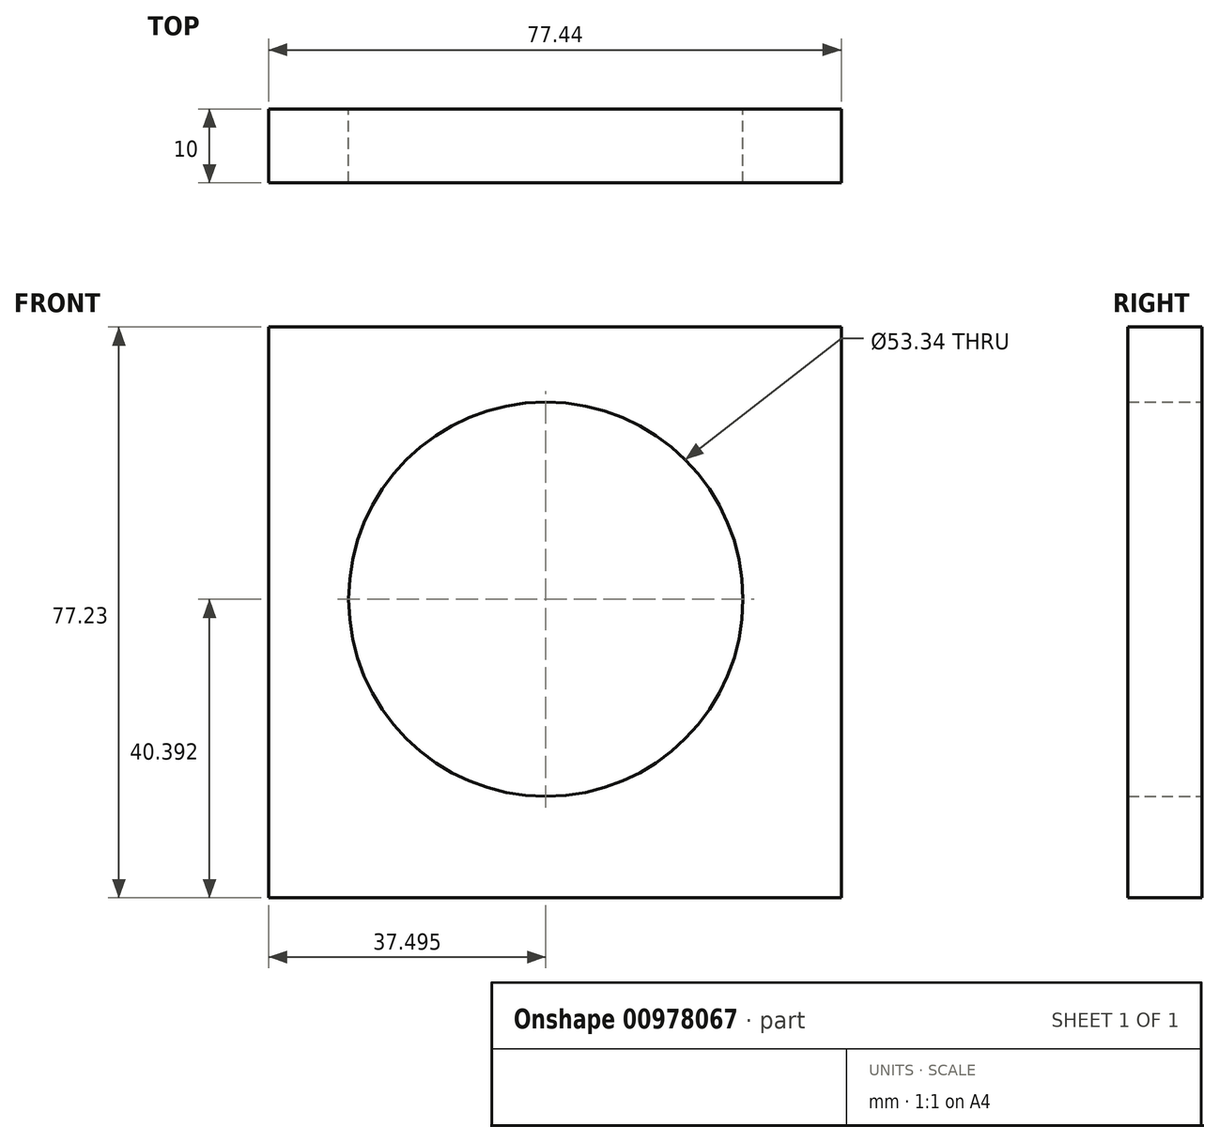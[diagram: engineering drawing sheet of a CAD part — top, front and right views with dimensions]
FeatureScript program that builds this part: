
annotation { "Feature Type Name" : "Feature", "Feature Type Description" : "" }
export const myFeature = defineFeature(function(context is Context, id is Id, definition is map)
    precondition{}
    {
        {
            var Q0;
            Q0=qCreatedBy(makeId("Front.planeOp"),FACE);
            var sketch = newSketch(context, id + "F0", { "sketchPlane" : qUnion([Q0])});
            skLineSegment(sketch, "E0.bottom", {"start": v(0, 0) * mm, "end": v(-77.44, 0) * mm});
            skLineSegment(sketch, "E0.top", {"start": v(0, -77.23) * mm, "end": v(-77.44, -77.23) * mm});
            skLineSegment(sketch, "E0.left", {"start": v(0, 0) * mm, "end": v(0, -77.23) * mm});
            skLineSegment(sketch, "E0.right", {"start": v(-77.44, 0) * mm, "end": v(-77.44, -77.23) * mm});
            skSolve(sketch);
        }
        {
            var Q0;
            Q0=makeQuery(id+"F0.imprint","IMPRINT",FACE,{"disambiguationData":[TD([[makeQuery(id+"F0.imprint","IMPRINT",EDGE,{"derivedFrom":sQuery(id+"F0.wireOp",EDGE,"E0.bottom")}),1.0]])]});
            var sketch = newSketch(context, id + "F1", { "sketchPlane" : qUnion([Q0])});
            skCircle(sketch, "E1", {"center": v(-39.95, -36.84) * mm, "radius": 26.67 * mm});
            skSolve(sketch);
        }
        {
            var Q0;
            Q0=makeQuery(id+"F1.imprint","IMPRINT",FACE,{"disambiguationData":[TD([[makeQuery(id+"F1.imprint","IMPRINT",EDGE,{"derivedFrom":sQuery(id+"F1.wireOp",EDGE,"E1")}),-1.0]])]});
            extrude(context, id + "F2", {"entities" : qUnion([Q0]), "depth" : 10 * mm, "offsetDistance" : 25.4 * mm});
        }
    });
